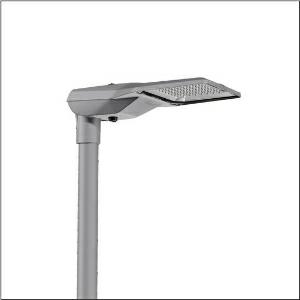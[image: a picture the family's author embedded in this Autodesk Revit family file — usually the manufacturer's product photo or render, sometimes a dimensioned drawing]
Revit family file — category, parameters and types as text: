
# Revit family: streetlight_sl_21_iq_midi___st0_5a_5xe3b31y08nb_abd3
name_source: partatom
category: Lighting Fixtures
units: mm (PartAtom-declared; Revit-internal decimal feet)

## family parameters
Cut with Voids When Loaded = No
Host = Face
Light Source = No
Part Type = Normal
Room Calculation Point = No
Round Connector Dimension = Use Diameter
Shared = No

## types (1)
- --- (1 x LED, 21550 lm, 136.6 W, 3000K)
    Apparent Load = 137 VA
    CIE Flux Codes = 43 76 97 100 100
    Color Rendering = 70
    Color Temperature = 3000K
    Default Elevation = 1800 mm
    Description = Streetlight SL 21 iQ midi, mast luminaire, primary light control with lens, of PMMA, primary optical cover: cover, of toughened safety glass, transparent, light distribution: ST0.5a, light emission: direct distribution, primary light characteristic: asymmetric, installation type: post-top, side-entry, LED, High Power LED, rated luminous flux: 21.550lm, luminous efficacy: 158lm/W, light colour: 730, colour temperature: 3000K, control gear: iQ-Street Remote, D4i with power reduction, control: pre-setting: logarithmic dimming characteristic, Street-Remote, Auto-Match, Temp-Guard, Lumen-Switch, Night-Set, Smart-Wire, Light-Fading, Desk-Remote (wireless, voltage-free reading and setting of iQ features in the workshop via application-optimized NFC function/RFID function), optimised constant luminous flux control (CLO 2.0), mains connection: 230..240V, AC, 50/60Hz, start of lifetime: 137W, end of service life: 144W, reduction: 61W, luminaire housing, of diecast aluminium, powder-coated, SITECO metallic grey (DB 702S), corrosivity category C5 high according to DIN EN ISO 12944, please order mast flange separately, inclination adjustable: 0°, 5°, 10°, 15°, sealing non-destructively replaceable, multi-level sealing system, length: 644mm, width: 335mm, height: 110mm, mast flange for spigot size: 42mm (side-entry): 5XC10008XM4, 60/48mm (side-entry/post-top): 5XC10108XM2, 76/60mm (side-entry/post-top): 5XC10108XM1, mounting height: 4..8m, Smart Interface below and above, protection rating (complete): IP66, insulation class (complete): insulation class II (safety insulation), certification: CE, ENEC, ENEC+, VDE, impact resistance: IK10, permissible operating ambient temperature for outdoor applications: -40..+50°C, standard-compliant lighting for roads and squares, packaging unit: 1 piece

Light Distribution: ST0.5a
    Height = 111 mm
    Lamp = 1 x LED
    Lamp Light Flux = 21550 lm
    Lamp Power = 136.6 W
    Lamp count = 1
    Length = 644 mm
    Luminous efficacy = 158 lm/W
    Manufacturer = Siteco
    ModVariant = No
    Model = 5XE3B31Y08NB
    Number of Poles = 1
    OnlyDefault = Yes
    Power Factor = 1
    Product Name = Streetlight SL 21 iQ midi | ST0.5a
    Product group = mast luminaire | pylon top
    ProductGroupID = 6100
    Protection Class = Protection class II
    Protection Degree = IP 66
    RLX_Detail_Level = 1
    RLX_Emergency_Light_Flux = 0 lm
    RLX_Emergency_Type = 0
    RLX_Emergency_Type_DB = No
    RlxData = <blob elided: 102345 chars, md5=9dc92dfe>
    Socket = socket
    Standby Power = 0 W
    System Light Flux = 21550 lm
    System Power = 137 W
    Type Comments = factory setting: luminous flux: 100 % | dim-lin: 254 | 733 mA
    Type Image = l_1004304.jpg
    URL = http://relux.com
    VarID = @adj_115921
    Voltage = 0 V
    Weight = 0.00 kg
    Width = 336 mm

## geometry (parser evidence)
native form markers: Blend x4, Sweep x12
no freeform markers — native parametric forms only
